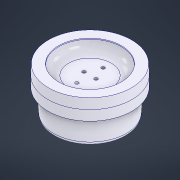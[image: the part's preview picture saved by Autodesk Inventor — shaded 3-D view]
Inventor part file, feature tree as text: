
AUTODESK INVENTOR PART (.ipt)
format: ipt  version: 2022 (Build 260153000, 153)  size: 211,968 bytes
history: native  units: mm
features: sketch x3, extrude x2, revolve x1, fillet x1, plane x1
ambient origin geometry x8: Origin, YZ Plane, XZ Plane, XY Plane, X Axis, Y Axis, Z Axis, Center Point
bodies: Solid1 (feature_tree)
feature tree (8):
  revolve  "Revolution1"  [1 undecoded]
  fillet  "Fillet1"  Radius=83.0mm
  extrude  "Extrusion1"  Depth=35.0mm
  extrude  "Extrusion2"  Depth=10.0mm
  plane  "Work Plane1"
  sketch  "Sketch1"  dims[d0=32.0mm d2=18.0mm d4=83.0mm]
  sketch  "Sketch3"  dims[d19=360.0deg d20=35.0mm]
  sketch  "Sketch4"  dims[d21=24.43461mm d22=10.0mm d44=16.580628mm d45=10.0mm d46=16.057029mm d47=10.0mm d48=73.5mm d49=16.057029mm d50=3.2mm d51=3.2mm d52=6.0mm d53=6.0mm d54=3.2mm d55=13.0mm d56=60.0mm d58=360.0deg d60=0.0mm d61=0.0mm d62=20.0mm d63=5.0mm d64=0.0mm d73=45.0mm]
note: 1 required parameter value undecoded (feature->parameter linkage not recoverable at this tier; creation-order binding heuristic only, values carry confidence <= 0.55)
